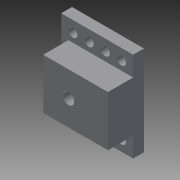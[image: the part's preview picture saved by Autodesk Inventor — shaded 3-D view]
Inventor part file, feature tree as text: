
AUTODESK INVENTOR PART (.ipt)
format: ipt  version: 2013 SP2 (Build 170200200, 200)  size: 146,432 bytes
history: native  units: in
note: dims shown in document units (in); Inventor stores cm internally (conversion verified against a paired STEP export)
features: extrude x4, sketch x4
ambient origin geometry x8: Origin, YZ Plane, XZ Plane, XY Plane, X Axis, Y Axis, Z Axis, Center Point
bodies: Solid1 (feature_tree)
feature tree (8):
  extrude  "Extrusion1"  Depth=0.9843in
  extrude  "Extrusion2"  Depth=0.4724in
  extrude  "Extrusion3"  Depth=0.1181in TaperAngle=0.0deg
  extrude  "Extrusion4"  Depth=0.1181in TaperAngle=0.0deg
  sketch  "Sketch1"  dims[d0=0.7874in d2=0.9843in]
  sketch  "Sketch2"  dims[d3=0.315in d4=0.4724in]
  sketch  "Sketch3"  dims[d5=0.1181in d6=0.1181in d7=0.0in]
  sketch  "Sketch4"  dims[d8=0.2756in d9=0.0in d10=0.1181in d11=0.0in d12=0.0984in d13=0.0984in d14=0.0984in d15=0.0984in d16=0.0984in d17=0.0984in d18=0.0984in d19=0.0984in d20=0.1772in d21=0.1772in d22=0.1772in d23=0.1181in d24=0.1181in d25=0.3937in d26=0.0in d27=0.126in d28=0.1575in]
